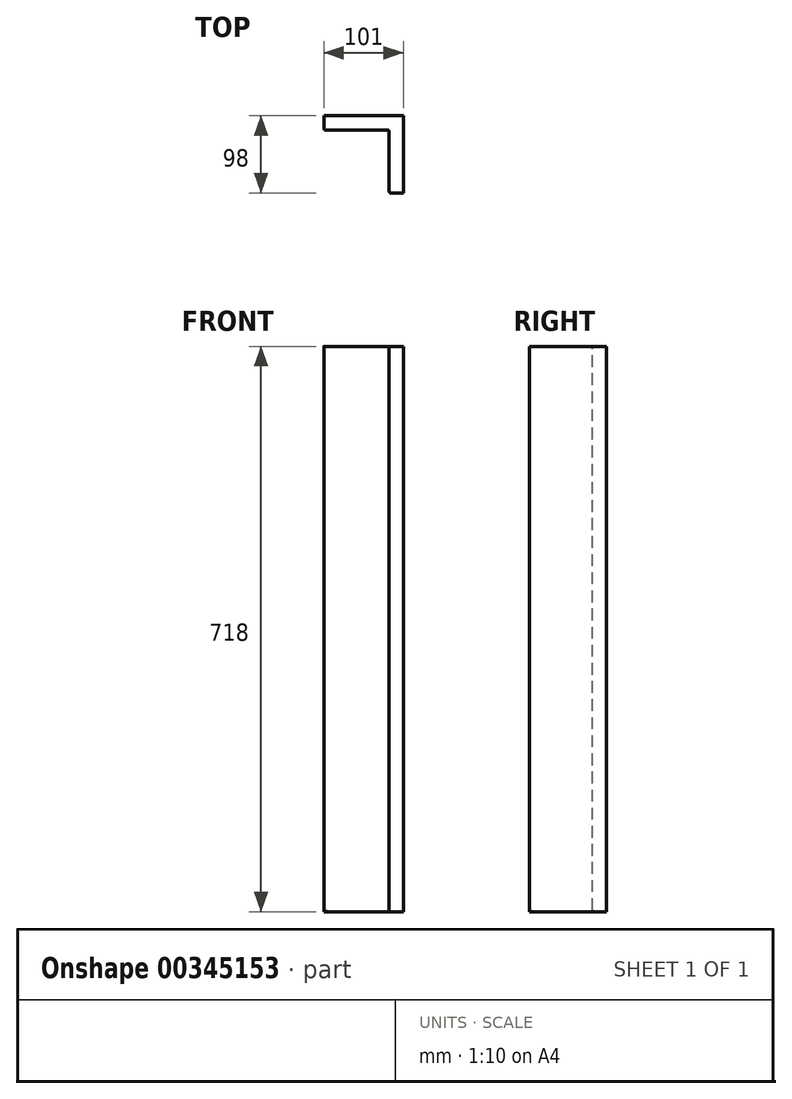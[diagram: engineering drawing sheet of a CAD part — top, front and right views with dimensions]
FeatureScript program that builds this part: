
annotation { "Feature Type Name" : "Feature", "Feature Type Description" : "" }
export const myFeature = defineFeature(function(context is Context, id is Id, definition is map)
    precondition{}
    {
        {
            var Q0;
            Q0=qCreatedBy(makeId("Front.planeOp"),FACE);
            var sketch = newSketch(context, id + "F0", { "sketchPlane" : qUnion([Q0])});
            skLineSegment(sketch, "E0.bottom", {"start": v(0, 0) * mm, "end": v(38.97, 0) * mm});
            skLineSegment(sketch, "E0.top", {"start": v(0, 53.4) * mm, "end": v(38.97, 53.4) * mm});
            skLineSegment(sketch, "E0.left", {"start": v(0, 0) * mm, "end": v(0, 53.4) * mm});
            skLineSegment(sketch, "E0.right", {"start": v(38.97, 0) * mm, "end": v(38.97, 53.4) * mm});
            skSolve(sketch);
        }
        {
            var Q0;
            Q0=makeQuery(id+"F0.imprint","IMPRINT",FACE,{"disambiguationData":[TD([[makeQuery(id+"F0.imprint","IMPRINT",EDGE,{"derivedFrom":sQuery(id+"F0.wireOp",EDGE,"E0.bottom")}),1.0]])]});
            extrude(context, id + "F1", {"entities" : qUnion([Q0]), "depth" : 18 * mm});
        }
        {
            var Q0;
            Q0=makeQuery(id+"F1.opExtrude","SWEPT_FACE",FACE,{"disambiguationData":[OSD([sQuery(id+"F0.wireOp",EDGE,"E0.left")])]});
            extrude(context, id + "F2", {"entities" : qUnion([Q0]), "operationType" : NewBodyOperationType.ADD, "oppositeDirection" : true, "depth" : 50 * mm});
        }
        {
            var Q0;
            {var subQ0=sQuery(id+"F0.wireOp",EDGE,"E0.bottom");Q0=makeQuery(id+"F2.boolean.opBoolean","MERGE",FACE,{"derivedFrom":[makeQuery(id+"F1.opExtrude","SWEPT_FACE",FACE,{"disambiguationData":[OSD([subQ0])]}),makeQuery(id+"F2.opExtrude","SWEPT_FACE",FACE,{"disambiguationData":[OSD([subQ0,sQuery(id+"F0.wireOp",EDGE,"E0.left")])]})]});}
            extrude(context, id + "F3", {"entities" : qUnion([Q0]), "operationType" : NewBodyOperationType.ADD, "oppositeDirection" : true, "depth" : 25 * mm});
        }
        {
            var Q0;
            {var subQ0=sQuery(id+"F0.wireOp",EDGE,"E0.bottom");Q0=makeQuery(id+"F2.boolean.opBoolean","MERGE",FACE,{"derivedFrom":[makeQuery(id+"F1.opExtrude","SWEPT_FACE",FACE,{"disambiguationData":[OSD([subQ0])]}),makeQuery(id+"F2.opExtrude","SWEPT_FACE",FACE,{"disambiguationData":[OSD([subQ0,sQuery(id+"F0.wireOp",EDGE,"E0.left")])]})]});}
            extrude(context, id + "F4", {"entities" : qUnion([Q0]), "operationType" : NewBodyOperationType.ADD, "oppositeDirection" : true, "depth" : 718 * mm});
        }
        {
            var Q0;
            {var subQ0=sQuery(id+"F0.wireOp",EDGE,"E0.left");var subQ1=sQuery(id+"F0.wireOp",EDGE,"E0.bottom");Q0=makeQuery(id+"F4.boolean.opBoolean","MERGE",FACE,{"derivedFrom":[makeQuery(id+"F2.boolean.opBoolean","MERGE",FACE,{"derivedFrom":[makeQuery(id+"F1.opExtrude","CAP_FACE",FACE,{"disambiguationData":[OSD([subQ1,sQuery(id+"F0.wireOp",EDGE,"E0.top"),subQ0,sQuery(id+"F0.wireOp",EDGE,"E0.right")])],"isStart":false}),makeQuery(id+"F2.opExtrude","SWEPT_FACE",FACE,{"disambiguationData":[OSD([subQ0]),TDD([makeQuery(id+"F1.opExtrude","CAP_EDGE",EDGE,{"disambiguationData":[OSD([subQ0])],"isStart":false})])]})]}),makeQuery(id+"F4.opExtrude","SWEPT_FACE",FACE,{"disambiguationData":[OSD([subQ1,subQ0]),TDD([makeQuery(id+"F2.boolean.opBoolean","MERGE",EDGE,{"derivedFrom":[makeQuery(id+"F1.opExtrude","CAP_EDGE",EDGE,{"disambiguationData":[OSD([subQ1])],"isStart":false}),makeQuery(id+"F2.opExtrude","SWEPT_EDGE",EDGE,{"disambiguationData":[OSD([subQ1,subQ0]),TDD([makeQuery(id+"F1.opExtrude","CAP_VERTEX",VERTEX,{"disambiguationData":[OSD([subQ1,subQ0])],"isStart":false})])]})]})])]})]});}
            var sketch = newSketch(context, id + "F5", { "sketchPlane" : qUnion([Q0])});
            skLineSegment(sketch, "E1.bottom", {"start": v(50, 718) * mm, "end": v(25, 718) * mm});
            skLineSegment(sketch, "E1.top", {"start": v(50, 0) * mm, "end": v(25, 0) * mm});
            skLineSegment(sketch, "E1.left", {"start": v(50, 718) * mm, "end": v(50, 0) * mm});
            skLineSegment(sketch, "E1.right", {"start": v(25, 718) * mm, "end": v(25, 0) * mm});
            skSolve(sketch);
        }
        {
            var Q0;
            Q0=makeQuery(id+"F5.imprint","IMPRINT",FACE,{"disambiguationData":[TD([[makeQuery(id+"F5.imprint","IMPRINT",EDGE,{"derivedFrom":sQuery(id+"F5.wireOp",EDGE,"E1.bottom")}),-1.0]])]});
            extrude(context, id + "F6", {"entities" : qUnion([Q0]), "operationType" : NewBodyOperationType.ADD, "depth" : 20 * mm});
        }
        {
            var Q0;
            Q0=makeQuery(id+"F6.opExtrude","SWEPT_FACE",FACE,{"disambiguationData":[OSD([sQuery(id+"F5.wireOp",EDGE,"E1.right")])]});
            extrude(context, id + "F7", {"entities" : qUnion([Q0]), "operationType" : NewBodyOperationType.REMOVE, "oppositeDirection" : true, "depth" : 7 * mm});
        }
        {
            var Q0;
            Q0=makeQuery(id+"F6.opExtrude","CAP_FACE",FACE,{"disambiguationData":[OSD([sQuery(id+"F5.wireOp",EDGE,"E1.bottom"),sQuery(id+"F5.wireOp",EDGE,"E1.top"),sQuery(id+"F5.wireOp",EDGE,"E1.left"),sQuery(id+"F5.wireOp",EDGE,"E1.right")])],"isStart":false});
            extrude(context, id + "F8", {"entities" : qUnion([Q0]), "operationType" : NewBodyOperationType.ADD, "depth" : 80 * mm});
        }
        {
            var Q0;
            Q0=makeQuery(id+"F8.opExtrude","CAP_FACE",FACE,{"disambiguationData":[OSD([sQuery(id+"F5.wireOp",EDGE,"E1.bottom"),sQuery(id+"F5.wireOp",EDGE,"E1.top"),sQuery(id+"F5.wireOp",EDGE,"E1.left"),sQuery(id+"F5.wireOp",EDGE,"E1.right")])],"isStart":false});
            extrude(context, id + "F9", {"entities" : qUnion([Q0]), "operationType" : NewBodyOperationType.REMOVE, "oppositeDirection" : true, "depth" : 20 * mm});
        }
        {
            var Q0;
            {var subQ0=sQuery(id+"F0.wireOp",EDGE,"E0.left");var subQ1=sQuery(id+"F0.wireOp",EDGE,"E0.bottom");Q0=makeQuery(id+"F4.boolean.opBoolean","MERGE",FACE,{"derivedFrom":[makeQuery(id+"F1.opExtrude","SWEPT_FACE",FACE,{"disambiguationData":[OSD([subQ0])]}),makeQuery(id+"F4.opExtrude","SWEPT_FACE",FACE,{"disambiguationData":[OSD([subQ1,subQ0]),TDD([makeQuery(id+"F1.opExtrude","SWEPT_EDGE",EDGE,{"disambiguationData":[OSD([subQ1,subQ0])]})])]})]});}
            extrude(context, id + "F10", {"entities" : qUnion([Q0]), "operationType" : NewBodyOperationType.ADD, "depth" : 70 * mm});
        }
        {
            var Q0;
            Q0=makeQuery(id+"F10.opExtrude","CAP_FACE",FACE,{"disambiguationData":[OSD([sQuery(id+"F0.wireOp",EDGE,"E0.bottom"),sQuery(id+"F0.wireOp",EDGE,"E0.left")])],"isStart":false});
            extrude(context, id + "F11", {"entities" : qUnion([Q0]), "operationType" : NewBodyOperationType.REMOVE, "oppositeDirection" : true, "depth" : 18 * mm});
        }
        {
            var Q0;
            Q0=makeQuery(id+"F11.boolean.opBoolean","COPY",FACE,{"derivedFrom":makeQuery(id+"F11.opExtrude","CAP_FACE",FACE,{"disambiguationData":[OSD([sQuery(id+"F0.wireOp",EDGE,"E0.bottom"),sQuery(id+"F0.wireOp",EDGE,"E0.left")])],"isStart":false})});
            extrude(context, id + "F12", {"entities" : qUnion([Q0]), "operationType" : NewBodyOperationType.REMOVE, "oppositeDirection" : true, "depth" : 1 * mm});
        }
        {
            var Q0;
            {var subQ0=sQuery(id+"F0.wireOp",EDGE,"E0.left");var subQ1=sQuery(id+"F0.wireOp",EDGE,"E0.bottom");var subQ2=makeQuery(id+"F1.opExtrude","CAP_VERTEX",VERTEX,{"disambiguationData":[OSD([subQ1,subQ0])],"isStart":false});var subQ3=makeQuery(id+"F1.opExtrude","CAP_EDGE",EDGE,{"disambiguationData":[OSD([subQ0])],"isStart":false});var subQ4=sQuery(id+"F5.wireOp",EDGE,"E1.right");Q0=makeQuery(id+"F10.boolean.opBoolean","MERGE",FACE,{"derivedFrom":[makeQuery(id+"F7.boolean.opBoolean","MERGE",FACE,{"derivedFrom":[makeQuery(id+"F4.boolean.opBoolean","MERGE",FACE,{"derivedFrom":[makeQuery(id+"F2.boolean.opBoolean","MERGE",FACE,{"derivedFrom":[makeQuery(id+"F1.opExtrude","CAP_FACE",FACE,{"disambiguationData":[OSD([subQ1,sQuery(id+"F0.wireOp",EDGE,"E0.top"),subQ0,sQuery(id+"F0.wireOp",EDGE,"E0.right")])],"isStart":false}),makeQuery(id+"F2.opExtrude","SWEPT_FACE",FACE,{"disambiguationData":[OSD([subQ0]),TDD([subQ3])]})]}),makeQuery(id+"F4.opExtrude","SWEPT_FACE",FACE,{"disambiguationData":[OSD([subQ1,subQ0]),TDD([makeQuery(id+"F2.boolean.opBoolean","MERGE",EDGE,{"derivedFrom":[makeQuery(id+"F1.opExtrude","CAP_EDGE",EDGE,{"disambiguationData":[OSD([subQ1])],"isStart":false}),makeQuery(id+"F2.opExtrude","SWEPT_EDGE",EDGE,{"disambiguationData":[OSD([subQ1,subQ0]),TDD([subQ2])]})]})])]})]}),makeQuery(id+"F7.opExtrude","SWEPT_FACE",FACE,{"disambiguationData":[OSD([subQ4]),TDD([makeQuery(id+"F6.opExtrude","CAP_EDGE",EDGE,{"disambiguationData":[OSD([subQ4])],"isStart":true})])]})]}),makeQuery(id+"F10.opExtrude","SWEPT_FACE",FACE,{"disambiguationData":[OSD([subQ1,subQ0]),TDD([makeQuery(id+"F4.boolean.opBoolean","MERGE",EDGE,{"derivedFrom":[subQ3,makeQuery(id+"F4.opExtrude","SWEPT_EDGE",EDGE,{"disambiguationData":[OSD([subQ1,subQ0]),TDD([subQ2])]})]})])]})]});}
            var Q1;
            {var subQ0=sQuery(id+"F5.wireOp",EDGE,"E1.right");Q1=makeQuery(id+"F8.boolean.opBoolean","MERGE",FACE,{"derivedFrom":[makeQuery(id+"F7.boolean.opBoolean","COPY",FACE,{"derivedFrom":makeQuery(id+"F7.opExtrude","CAP_FACE",FACE,{"disambiguationData":[OSD([subQ0])],"isStart":false})}),makeQuery(id+"F8.opExtrude","SWEPT_FACE",FACE,{"disambiguationData":[OSD([subQ0])]})]});}
            var Q2;
            Q2=makeQuery(id+"F9.boolean.opBoolean","COPY",EDGE,{"derivedFrom":makeQuery(id+"F9.opExtrude","CAP_EDGE",EDGE,{"disambiguationData":[OSD([sQuery(id+"F5.wireOp",EDGE,"E1.bottom")])],"isStart":false})});
            var Q3;
            {var subQ0=sQuery(id+"F0.wireOp",EDGE,"E0.left");var subQ1=sQuery(id+"F0.wireOp",EDGE,"E0.bottom");Q3=makeQuery(id+"F12.boolean.opBoolean","COPY",EDGE,{"derivedFrom":makeQuery(id+"F12.opExtrude","CAP_EDGE",EDGE,{"disambiguationData":[OSD([subQ1,subQ0]),TDD([makeQuery(id+"F11.boolean.opBoolean","COPY",EDGE,{"derivedFrom":makeQuery(id+"F11.opExtrude","CAP_EDGE",EDGE,{"disambiguationData":[OSD([subQ1,subQ0]),TDD([makeQuery(id+"F10.opExtrude","CAP_EDGE",EDGE,{"disambiguationData":[OSD([subQ1,subQ0]),TDD([makeQuery(id+"F4.opExtrude","CAP_EDGE",EDGE,{"disambiguationData":[OSD([subQ1,subQ0]),TDD([makeQuery(id+"F1.opExtrude","SWEPT_EDGE",EDGE,{"disambiguationData":[OSD([subQ1,subQ0])]})])],"isStart":false})])],"isStart":false})])],"isStart":false})})])],"isStart":false})});}
            fillet(context, id + "F13", {"entities" : qUnion([Q0, Q1, Q2, Q3]), "radius" : 2 * mm, "tangentPropagation" : true, "allowEdgeOverflow" : false});
        }
    });
